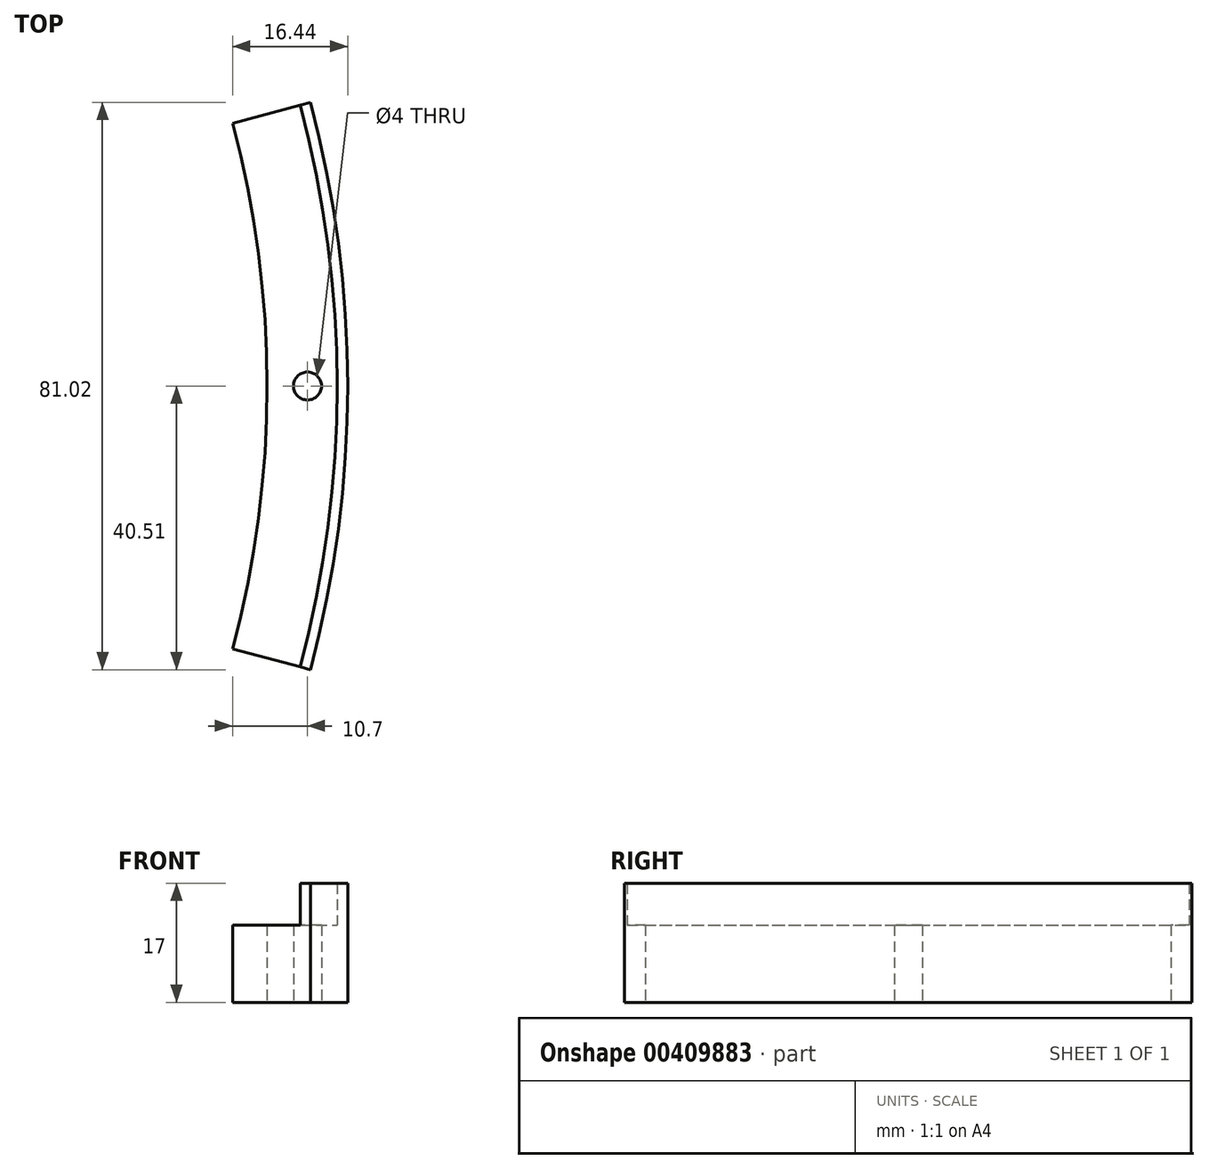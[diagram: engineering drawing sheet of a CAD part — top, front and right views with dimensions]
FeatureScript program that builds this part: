
annotation { "Feature Type Name" : "Feature", "Feature Type Description" : "" }
export const myFeature = defineFeature(function(context is Context, id is Id, definition is map)
    precondition{}
    {
        {
            var Q0;
            Q0=qCreatedBy(makeId("Top.planeOp"),FACE);
            var sketch = newSketch(context, id + "F0", { "sketchPlane" : qUnion([Q0])});
            skCircle(sketch, "E0", {"center": v(0, 0) * mm, "radius": 156.5 * mm});
            skCircle(sketch, "E1", {"center": v(0, 0) * mm, "radius": 155 * mm});
            skSolve(sketch);
        }
        {
            var Q0;
            Q0=makeQuery(id+"F0.imprint","IMPRINT",FACE,{"disambiguationData":[TD([[makeQuery(id+"F0.imprint","IMPRINT",EDGE,{"derivedFrom":sQuery(id+"F0.wireOp",EDGE,"E1")}),1.0]])]});
            var sketch = newSketch(context, id + "F1", { "sketchPlane" : qUnion([Q0])});
            skCircle(sketch, "E2", {"center": v(0, 0) * mm, "radius": 145 * mm});
            skCircle(sketch, "E3", {"center": v(0, 0) * mm, "radius": 156.5 * mm});
            skCircle(sketch, "E4", {"center": v(0, 150.76) * mm, "radius": 2 * mm});
            skCircle(sketch, "E5.1.0", {"center": v(-75.38, 130.56) * mm, "radius": 2 * mm});
            skCircle(sketch, "E5.2.0", {"center": v(-130.56, 75.38) * mm, "radius": 2 * mm});
            skCircle(sketch, "E5.3.0", {"center": v(-150.76, 0) * mm, "radius": 2 * mm});
            skCircle(sketch, "E5.4.0", {"center": v(-130.56, -75.38) * mm, "radius": 2 * mm});
            skCircle(sketch, "E5.5.0", {"center": v(-75.38, -130.56) * mm, "radius": 2 * mm});
            skCircle(sketch, "E5.6.0", {"center": v(0, -150.76) * mm, "radius": 2 * mm});
            skCircle(sketch, "E5.7.0", {"center": v(75.38, -130.56) * mm, "radius": 2 * mm});
            skCircle(sketch, "E5.8.0", {"center": v(130.56, -75.38) * mm, "radius": 2 * mm});
            skCircle(sketch, "E5.9.0", {"center": v(150.76, 0) * mm, "radius": 2 * mm});
            skCircle(sketch, "E5.10.0", {"center": v(130.56, 75.38) * mm, "radius": 2 * mm});
            skCircle(sketch, "E5.11.0", {"center": v(75.38, 130.56) * mm, "radius": 2 * mm});
            skSolve(sketch);
        }
        {
            var Q0;
            Q0=qSketchRegion(id+"F0",true);
            extrude(context, id + "F2", {"entities" : qUnion([Q0]), "depth" : 17 * mm});
        }
        {
            var Q0;
            Q0=qSketchRegion(id+"F1",true);
            extrude(context, id + "F3", {"entities" : qUnion([Q0]), "operationType" : NewBodyOperationType.ADD, "depth" : 11 * mm});
        }
        {
            var Q0;
            Q0=qCreatedBy(makeId("Top.planeOp"),FACE);
            var sketch = newSketch(context, id + "F4", { "sketchPlane" : qUnion([Q0])});
            skLineSegment(sketch, "E6", {"start": v(0, 0) * mm, "end": v(186.3, 49.92) * mm});
            skLineSegment(sketch, "E7", {"start": v(186.3, 49.92) * mm, "end": v(186.3, -49.92) * mm});
            skLineSegment(sketch, "E8", {"start": v(186.3, -49.92) * mm, "end": v(0, 0) * mm});
            skSolve(sketch);
        }
        {
            var Q0;
            Q0=qSketchRegion(id+"F4",true);
            extrude(context, id + "F5", {"entities" : qUnion([Q0]), "operationType" : NewBodyOperationType.INTERSECT, "depth" : 25 * mm});
        }
    });
